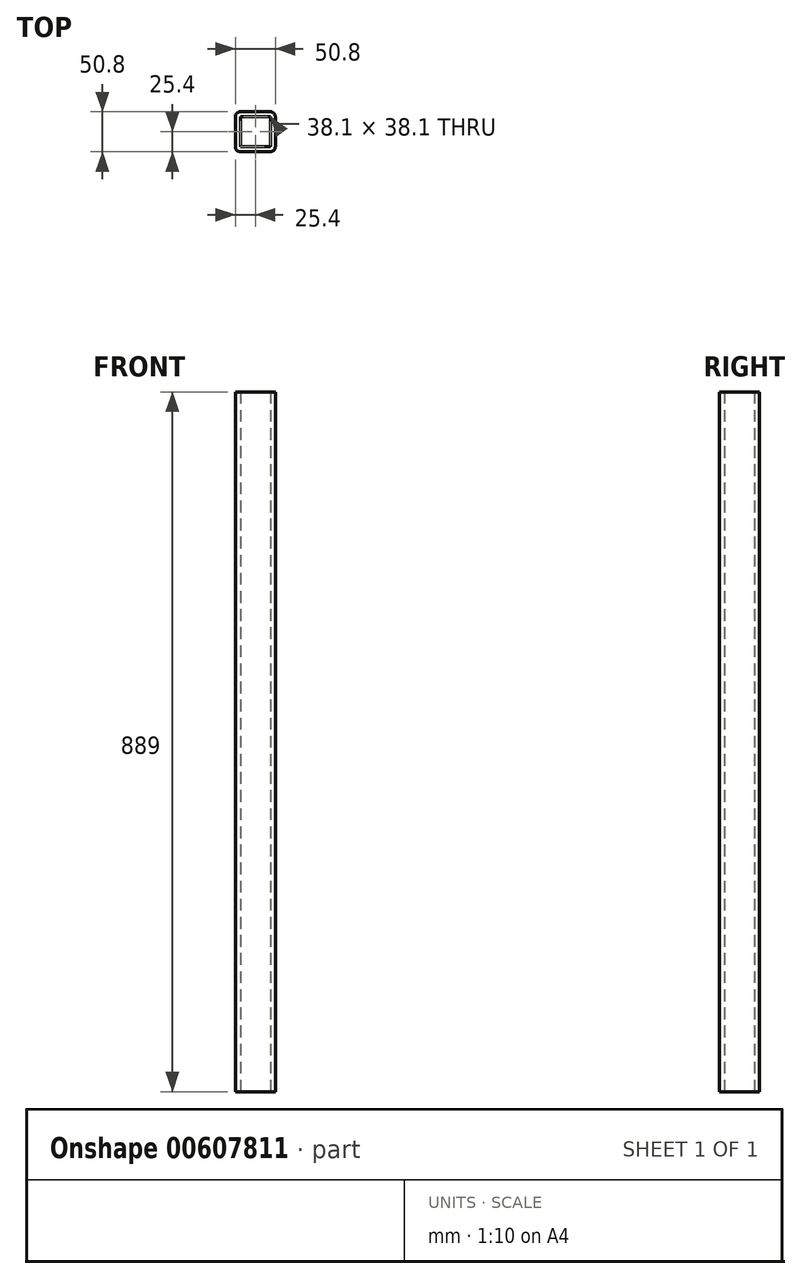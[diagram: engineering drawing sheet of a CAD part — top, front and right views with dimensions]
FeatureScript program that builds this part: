
annotation { "Feature Type Name" : "Feature", "Feature Type Description" : "" }
export const myFeature = defineFeature(function(context is Context, id is Id, definition is map)
    precondition{}
    {
        {
            var Q0;
            Q0=qCreatedBy(makeId("Top.planeOp"),FACE);
            var sketch = newSketch(context, id + "F0", { "sketchPlane" : qUnion([Q0])});
            skLineSegment(sketch, "E0.bottom", {"start": v(6.35, 0) * mm, "end": v(44.45, 0) * mm});
            skLineSegment(sketch, "E0.top", {"start": v(6.35, 50.8) * mm, "end": v(44.45, 50.8) * mm});
            skLineSegment(sketch, "E0.left", {"start": v(0, 6.35) * mm, "end": v(0, 44.45) * mm});
            skLineSegment(sketch, "E0.right", {"start": v(50.8, 6.35) * mm, "end": v(50.8, 44.45) * mm});
            skPoint(sketch, "E1.visualSharp", {"position": v(50.8, 50.8) * mm});
            skArc(sketch, "E1.filletArc", {"start": v(50.8, 44.45) * mm, "mid": v(48.94, 48.94) * mm, "end": v(44.45, 50.8) * mm});
            skPoint(sketch, "E2.visualSharp", {"position": v(50.8, 0) * mm});
            skArc(sketch, "E2.filletArc", {"start": v(44.45, 0) * mm, "mid": v(48.94, 1.86) * mm, "end": v(50.8, 6.35) * mm});
            skPoint(sketch, "E3.visualSharp", {"position": v(0, 0) * mm});
            skArc(sketch, "E3.filletArc", {"start": v(0, 6.35) * mm, "mid": v(1.86, 1.86) * mm, "end": v(6.35, 0) * mm});
            skPoint(sketch, "E4.visualSharp", {"position": v(0, 50.8) * mm});
            skArc(sketch, "E4.filletArc", {"start": v(6.35, 50.8) * mm, "mid": v(1.86, 48.94) * mm, "end": v(0, 44.45) * mm});
            skSolve(sketch);
        }
        {
            var Q0;
            Q0 = qSketchRegion(id + "F0", true);
            extrude(context, id + "F1", {"entities" : qUnion([Q0]), "depth" : 889 * mm, "offsetDistance" : 25.4 * mm});
        }
        {
            var Q0;
            Q0=makeQuery(id+"F1.opExtrude","CAP_FACE",FACE,{"disambiguationData":[OSD([sQuery(id+"F0.wireOp",EDGE,"E0.bottom"),sQuery(id+"F0.wireOp",EDGE,"E0.top"),sQuery(id+"F0.wireOp",EDGE,"E0.left"),sQuery(id+"F0.wireOp",EDGE,"E0.right"),sQuery(id+"F0.wireOp",EDGE,"E1.filletArc"),sQuery(id+"F0.wireOp",EDGE,"E2.filletArc"),sQuery(id+"F0.wireOp",EDGE,"E3.filletArc"),sQuery(id+"F0.wireOp",EDGE,"E4.filletArc")])],"isStart":false});
            var Q1;
            Q1=makeQuery(id+"F1.opExtrude","CAP_FACE",FACE,{"disambiguationData":[OSD([sQuery(id+"F0.wireOp",EDGE,"E0.bottom"),sQuery(id+"F0.wireOp",EDGE,"E0.top"),sQuery(id+"F0.wireOp",EDGE,"E0.left"),sQuery(id+"F0.wireOp",EDGE,"E0.right"),sQuery(id+"F0.wireOp",EDGE,"E1.filletArc"),sQuery(id+"F0.wireOp",EDGE,"E2.filletArc"),sQuery(id+"F0.wireOp",EDGE,"E3.filletArc"),sQuery(id+"F0.wireOp",EDGE,"E4.filletArc")])],"isStart":true});
            shell(context, id + "F2", {"entities" : qUnion([Q0, Q1]), "thickness" : 6.35 * mm});
        }
    });
